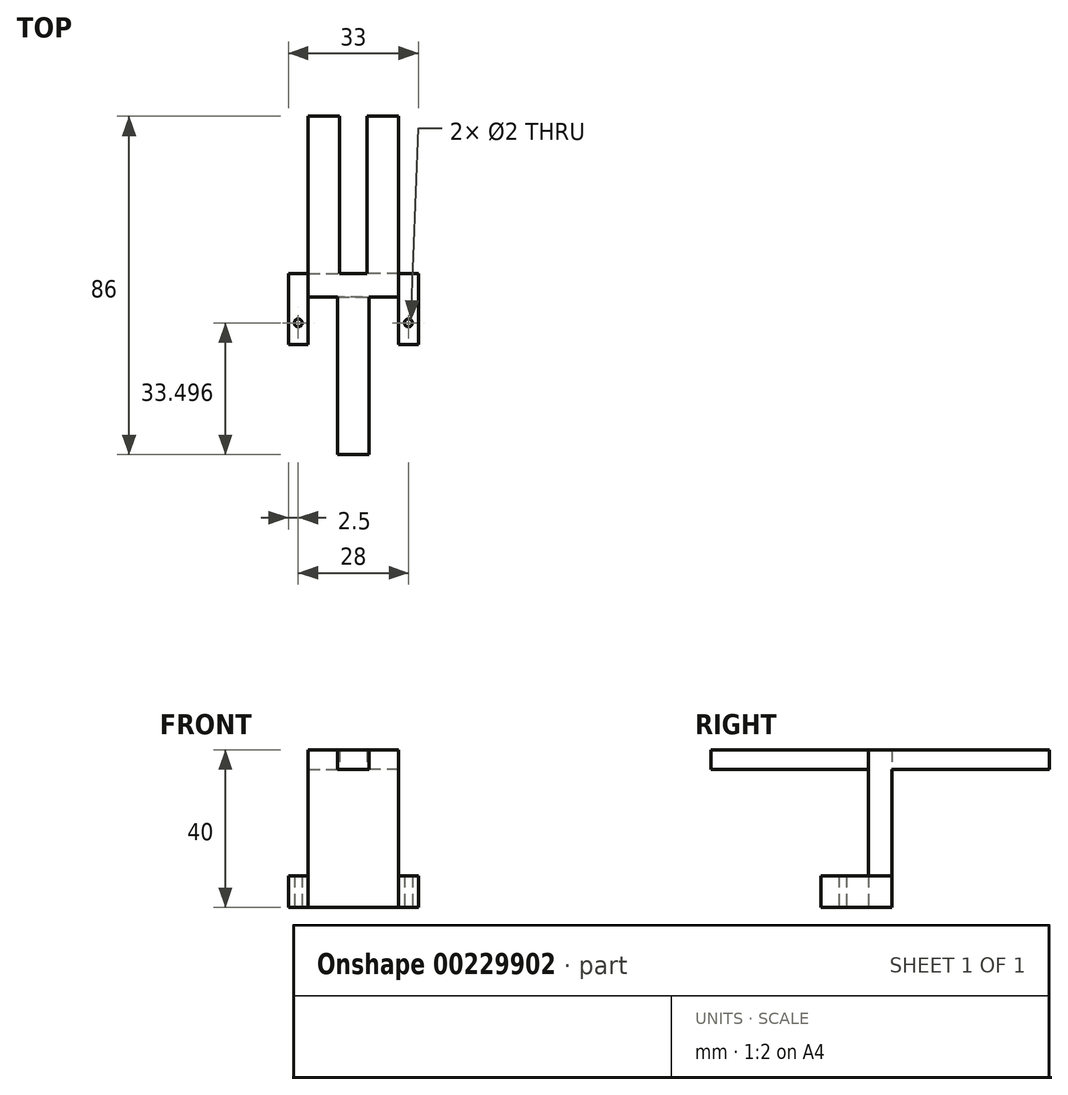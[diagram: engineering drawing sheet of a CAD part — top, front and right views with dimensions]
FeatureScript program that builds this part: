
annotation { "Feature Type Name" : "Feature", "Feature Type Description" : "" }
export const myFeature = defineFeature(function(context is Context, id is Id, definition is map)
    precondition{}
    {
        {
            var Q0;
            Q0=qCreatedBy(makeId("Top.planeOp"),FACE);
            var sketch = newSketch(context, id + "F0", { "sketchPlane" : qUnion([Q0])});
            skLineSegment(sketch, "E0.bottom", {"start": v(11.5, 7.79) * mm, "end": v(-11.5, 7.79) * mm});
            skLineSegment(sketch, "E0.top", {"start": v(11.5, 1.79) * mm, "end": v(-11.5, 1.79) * mm});
            skLineSegment(sketch, "E0.left", {"start": v(11.5, 7.79) * mm, "end": v(11.5, 1.79) * mm});
            skLineSegment(sketch, "E0.right", {"start": v(-11.5, 7.79) * mm, "end": v(-11.5, 1.79) * mm});
            skLineSegment(sketch, "E1.bottom", {"start": v(-11.5, 7.79) * mm, "end": v(-16.5, 7.79) * mm});
            skLineSegment(sketch, "E1.top", {"start": v(-11.5, -10.21) * mm, "end": v(-16.5, -10.21) * mm});
            skLineSegment(sketch, "E1.left", {"start": v(-11.5, 7.79) * mm, "end": v(-11.5, -10.21) * mm});
            skLineSegment(sketch, "E1.right", {"start": v(-16.5, 7.79) * mm, "end": v(-16.5, -10.21) * mm});
            skLineSegment(sketch, "E2.bottom", {"start": v(11.5, 7.79) * mm, "end": v(16.5, 7.79) * mm});
            skLineSegment(sketch, "E2.top", {"start": v(11.5, -10.21) * mm, "end": v(16.5, -10.21) * mm});
            skLineSegment(sketch, "E2.left", {"start": v(11.5, 7.79) * mm, "end": v(11.5, -10.21) * mm});
            skLineSegment(sketch, "E2.right", {"start": v(16.5, 7.79) * mm, "end": v(16.5, -10.21) * mm});
            skCircle(sketch, "E3", {"center": v(-14, -4.71) * mm, "radius": 1 * mm});
            skCircle(sketch, "E4", {"center": v(14, -4.71) * mm, "radius": 1 * mm});
            skSolve(sketch);
        }
        {
            var Q0;
            {var subQ3=sQuery(id+"F0.wireOp",EDGE,"E1.bottom");Q0=makeQuery(id+"F0.imprint","IMPRINT",FACE,{"disambiguationData":[TD([[makeQuery(id+"F0.imprint","IMPRINT",EDGE,{"derivedFrom":subQ3}),1.0]])]});}
            var Q1;
            {var subQ3=sQuery(id+"F0.wireOp",EDGE,"E2.bottom");Q1=makeQuery(id+"F0.imprint","IMPRINT",FACE,{"disambiguationData":[TD([[makeQuery(id+"F0.imprint","IMPRINT",EDGE,{"derivedFrom":subQ3}),-1.0]])]});}
            extrude(context, id + "F1", {"entities" : qUnion([Q0, Q1]), "depth" : 8 * mm});
        }
        {
            var Q0;
            {var subQ0=sQuery(id+"F0.wireOp",EDGE,"E0.bottom");Q0=makeQuery(id+"F0.imprint","IMPRINT",FACE,{"disambiguationData":[TD([[makeQuery(id+"F0.imprint","IMPRINT",EDGE,{"derivedFrom":subQ0}),1.0]])]});}
            extrude(context, id + "F2", {"entities" : qUnion([Q0]), "depth" : 40 * mm});
        }
        {
            var Q0;
            Q0=qCreatedBy(makeId("Top.planeOp"),FACE);
            var sketch = newSketch(context, id + "F3", { "sketchPlane" : qUnion([Q0])});
            skLineSegment(sketch, "E5.bottom", {"start": v(-11.5, 7.79) * mm, "end": v(-3.5, 7.79) * mm});
            skLineSegment(sketch, "E5.top", {"start": v(-11.5, 47.79) * mm, "end": v(-3.5, 47.79) * mm});
            skLineSegment(sketch, "E5.left", {"start": v(-11.5, 7.79) * mm, "end": v(-11.5, 47.79) * mm});
            skLineSegment(sketch, "E5.right", {"start": v(-3.5, 7.79) * mm, "end": v(-3.5, 47.79) * mm});
            skLineSegment(sketch, "E6.bottom", {"start": v(11.5, 7.79) * mm, "end": v(3.5, 7.79) * mm});
            skLineSegment(sketch, "E6.top", {"start": v(11.5, 47.79) * mm, "end": v(3.5, 47.79) * mm});
            skLineSegment(sketch, "E6.left", {"start": v(11.5, 7.79) * mm, "end": v(11.5, 47.79) * mm});
            skLineSegment(sketch, "E6.right", {"start": v(3.5, 7.79) * mm, "end": v(3.5, 47.79) * mm});
            skLineSegment(sketch, "E7.bottom", {"start": v(-4, 1.79) * mm, "end": v(4, 1.79) * mm});
            skLineSegment(sketch, "E7.top", {"start": v(-4, -38.21) * mm, "end": v(4, -38.21) * mm});
            skLineSegment(sketch, "E7.left", {"start": v(-4, 1.79) * mm, "end": v(-4, -38.21) * mm});
            skLineSegment(sketch, "E7.right", {"start": v(4, 1.79) * mm, "end": v(4, -38.21) * mm});
            skSolve(sketch);
        }
        {
            var Q0;
            Q0 = qSketchRegion(id + "F3", true);
            extrude(context, id + "F4", {"entities" : qUnion([Q0]), "operationType" : NewBodyOperationType.ADD, "depth" : 40 * mm, "hasSecondDirection" : true, "secondDirectionOppositeDirection" : false, "secondDirectionDepth" : 35 * mm});
        }
    });
